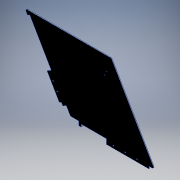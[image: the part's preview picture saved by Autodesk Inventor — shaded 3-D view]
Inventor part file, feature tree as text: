
AUTODESK INVENTOR PART (.ipt)
format: ipt  version: 2019.4 (Build 234330000, 330)  size: 224,768 bytes
history: native  units: mm
features: sketch x7, extrude x6, fillet x4
ambient origin geometry x8: Origin, YZ Plane, XZ Plane, XY Plane, X Axis, Y Axis, Z Axis, Center Point
bodies: Body1 (feature_tree)
feature tree (17):
  extrude  "Extrusion6"  Depth=3.0mm TaperAngle=0.0deg
  extrude  "Extrusion7"  TaperAngle=120.0deg  [1 undecoded]
  extrude  "Extrusion8"  Depth=3.0mm
  fillet  "Fillet1"  [1 undecoded]
  fillet  "Fillet2"  Radius=35.0mm
  fillet  "Fillet3"  Radius=3.0mm
  fillet  "Fillet4"  Radius=100.0mm
  extrude  "Extrusion12"  TaperAngle=30.0deg  [1 undecoded]
  extrude  "Extrusion13"  TaperAngle=60.0deg  [1 undecoded]
  extrude  "Extrusion14"  TaperAngle=30.0deg  [1 undecoded]
  sketch  "Sketch16"  dims[d76=3.5mm d77=20.0mm d78=90.0deg d79=3.5mm d80=3.0mm d81=0.0mm d82=5.0mm d83=2.0mm d84=2.0mm d85=2.0mm d123=10.0mm d124=103.0mm d125=120.0deg d126=10.0mm d127=115.0mm d128=180.0mm d129=10.0mm d130=3.0mm d131=0.0mm d132=0.0mm d133=184.0mm d134=11.0mm d135=9.0mm d136=106.0mm d137=11.0mm d138=3.0mm d139=0.0mm d140=50.0mm d141=5.5mm d142=30.0mm d144=50.0mm d145=10.0mm d147=10.0mm d149=35.0mm d150=120.0deg d151=5.5mm d152=20.0mm d154=35.0mm d155=10.0mm d157=10.0mm d159=3.0mm d160=0.0mm d161=545.0mm d162=330.0mm]
  sketch  "Sketch7"  dims[d56=365.0mm d58=3.0mm d59=0.0mm]
  sketch  "Sketch8"  dims[d60=90.0mm d61=120.0deg]
  sketch  "Sketch9"  dims[d62=35.0mm d63=90.0mm d64=0.0mm d65=35.0mm d66=3.0mm d67=0.0mm d69=100.0mm]
  sketch  "Sketch13"  dims[d70=90.0deg d71=30.0deg]
  sketch  "Sketch14"  dims[d72=305.0mm d73=60.0deg]
  sketch  "Sketch15"  dims[d74=13.0mm d75=30.0deg]
note: 5 required parameter values undecoded (feature->parameter linkage not recoverable at this tier; creation-order binding heuristic only, values carry confidence <= 0.55)
